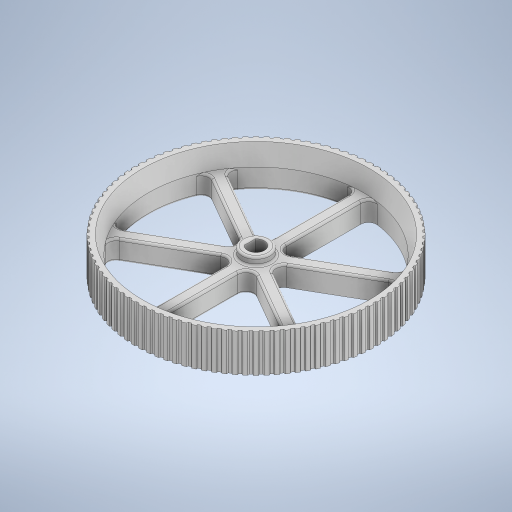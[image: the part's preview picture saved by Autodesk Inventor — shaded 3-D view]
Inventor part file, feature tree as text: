
AUTODESK INVENTOR PART (.ipt)
format: ipt  version: 2024.2 (Build 282272000, 272)  size: 1,016,320 bytes
history: native  units: mm
features: sketch x3, extrude x3, fillet x2, revolve x1
ambient origin geometry x8: Origin, YZ Plane, XZ Plane, XY Plane, X Axis, Y Axis, Z Axis, Center Point
bodies: Solid1 (feature_tree)
feature tree (9):
  revolve  "Revolution1"  [1 undecoded]
  sketch  "Sketch3"  dims[d3=30.0mm d4=360.0deg]
  extrude  "Extrusion1"  TaperAngle=360.0deg  [1 undecoded]
  extrude  "Extrusion2"  Depth=0.5mm
  extrude  "Extrusion3"  Depth=0.5mm
  fillet  "Fillet1"  Radius=7.0mm
  fillet  "Fillet2"  Radius=3.0mm
  sketch  "Sketch2"  dims[d0=3.0mm d2=5.0mm]
  sketch  "Sketch4"  dims[d5=4.2mm d6=1.6mm d7=15.0mm d8=7.0mm d9=3.0mm d10=1.5mm d11=60.0mm d13=360.0deg d15=5.0mm d16=0.0mm d17=7.0mm d18=0.0mm d19=120.0deg d20=120.0deg d21=1.6mm d22=1.0mm d23=0.5mm d24=1000.0mm d26=360.0deg d28=0.0mm d29=0.0mm d30=2.0mm d31=0.5mm d37=1.5mm d38=9.5mm d32=0.0mm d33=0.0mm d34=0.0mm d35=0.0mm]
note: 2 required parameter values undecoded (feature->parameter linkage not recoverable at this tier; creation-order binding heuristic only, values carry confidence <= 0.55)